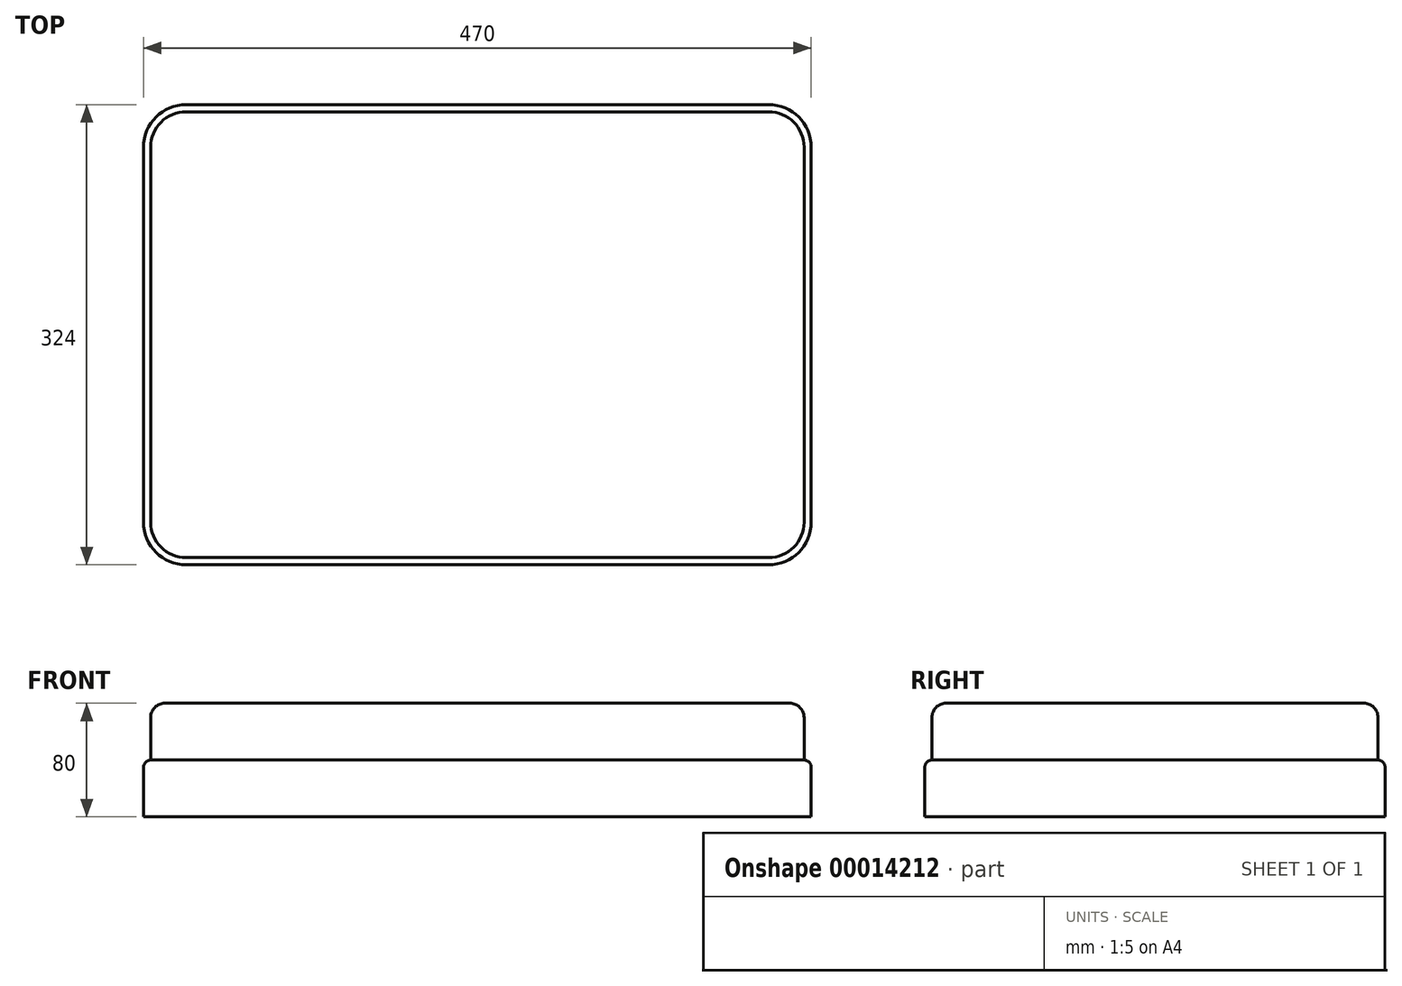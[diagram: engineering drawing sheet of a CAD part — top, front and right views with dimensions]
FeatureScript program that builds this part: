
annotation { "Feature Type Name" : "Feature", "Feature Type Description" : "" }
export const myFeature = defineFeature(function(context is Context, id is Id, definition is map)
    precondition{}
    {
        {
            var Q0;
            Q0=qCreatedBy(makeId("Top.planeOp"),FACE);
            var sketch = newSketch(context, id + "F0", { "sketchPlane" : qUnion([Q0])});
            skLineSegment(sketch, "E0.bottom", {"start": v(-205, 162) * mm, "end": v(205, 162) * mm});
            skLineSegment(sketch, "E0.top", {"start": v(-205, -162) * mm, "end": v(205, -162) * mm});
            skLineSegment(sketch, "E0.left", {"start": v(-235, 132) * mm, "end": v(-235, -132) * mm});
            skLineSegment(sketch, "E0.right", {"start": v(235, 132) * mm, "end": v(235, -132) * mm});
            skPoint(sketch, "E1", {"position": v(0, 162) * mm});
            skPoint(sketch, "E2", {"position": v(235, 0) * mm});
            skPoint(sketch, "E3.visualSharp", {"position": v(-235, -162) * mm});
            skArc(sketch, "E3.filletArc", {"start": v(-235, -132) * mm, "mid": v(-226.21, -153.21) * mm, "end": v(-205, -162) * mm});
            skPoint(sketch, "E4.visualSharp", {"position": v(235, -162) * mm});
            skArc(sketch, "E4.filletArc", {"start": v(205, -162) * mm, "mid": v(226.21, -153.21) * mm, "end": v(235, -132) * mm});
            skPoint(sketch, "E5.visualSharp", {"position": v(235, 162) * mm});
            skArc(sketch, "E5.filletArc", {"start": v(235, 132) * mm, "mid": v(226.21, 153.21) * mm, "end": v(205, 162) * mm});
            skPoint(sketch, "E6.visualSharp", {"position": v(-235, 162) * mm});
            skArc(sketch, "E6.filletArc", {"start": v(-205, 162) * mm, "mid": v(-226.21, 153.21) * mm, "end": v(-235, 132) * mm});
            skSolve(sketch);
        }
        {
            var Q0;
            Q0=qSketchRegion(id+"F0",true);
            extrude(context, id + "F1", {"entities" : qUnion([Q0]), "depth" : 40 * mm});
        }
        {
            var Q0;
            Q0=makeQuery(id+"F1.opExtrude","CAP_EDGE",EDGE,{"disambiguationData":[OSD([sQuery(id+"F0.wireOp",EDGE,"E0.top")])],"isStart":false});
            fillet(context, id + "F2", {"entities" : qUnion([Q0]), "radius" : 5 * mm, "tangentPropagation" : true, "allowEdgeOverflow" : false});
        }
        {
            var Q0;
            Q0=makeQuery(id+"F1.opExtrude","CAP_FACE",FACE,{"disambiguationData":[OSD([sQuery(id+"F0.wireOp",EDGE,"E0.bottom"),sQuery(id+"F0.wireOp",EDGE,"E0.top"),sQuery(id+"F0.wireOp",EDGE,"E0.left"),sQuery(id+"F0.wireOp",EDGE,"E0.right"),sQuery(id+"F0.wireOp",EDGE,"E3.filletArc"),sQuery(id+"F0.wireOp",EDGE,"E4.filletArc"),sQuery(id+"F0.wireOp",EDGE,"E5.filletArc"),sQuery(id+"F0.wireOp",EDGE,"E6.filletArc")])],"isStart":false});
            var sketch = newSketch(context, id + "F3", { "sketchPlane" : qUnion([Q0])});
            skLineSegment(sketch, "E7.bottom", {"start": v(-205, -157) * mm, "end": v(205, -157) * mm});
            skLineSegment(sketch, "E7.top", {"start": v(-205, 157) * mm, "end": v(205, 157) * mm});
            skLineSegment(sketch, "E7.left", {"start": v(-230, -132) * mm, "end": v(-230, 132) * mm});
            skLineSegment(sketch, "E7.right", {"start": v(230, -132) * mm, "end": v(230, 132) * mm});
            skPoint(sketch, "E8.visualSharp", {"position": v(-230, 157) * mm});
            skArc(sketch, "E8.filletArc", {"start": v(-205, 157) * mm, "mid": v(-222.68, 149.68) * mm, "end": v(-230, 132) * mm});
            skPoint(sketch, "E9.visualSharp", {"position": v(230, 157) * mm});
            skArc(sketch, "E9.filletArc", {"start": v(230, 132) * mm, "mid": v(222.68, 149.68) * mm, "end": v(205, 157) * mm});
            skPoint(sketch, "E10.visualSharp", {"position": v(230, -157) * mm});
            skArc(sketch, "E10.filletArc", {"start": v(205, -157) * mm, "mid": v(222.68, -149.68) * mm, "end": v(230, -132) * mm});
            skPoint(sketch, "E11.visualSharp", {"position": v(-230, -157) * mm});
            skArc(sketch, "E11.filletArc", {"start": v(-230, -132) * mm, "mid": v(-222.68, -149.68) * mm, "end": v(-205, -157) * mm});
            skSolve(sketch);
        }
        {
            var Q0;
            Q0=qSketchRegion(id+"F3",true);
            extrude(context, id + "F4", {"entities" : qUnion([Q0]), "depth" : 40 * mm});
        }
        {
            var Q0;
            Q0=makeQuery(id+"F4.opExtrude","CAP_EDGE",EDGE,{"disambiguationData":[OSD([sQuery(id+"F3.wireOp",EDGE,"E7.bottom")])],"isStart":false});
            fillet(context, id + "F5", {"entities" : qUnion([Q0]), "radius" : 10 * mm, "tangentPropagation" : true, "allowEdgeOverflow" : false});
        }
    });
